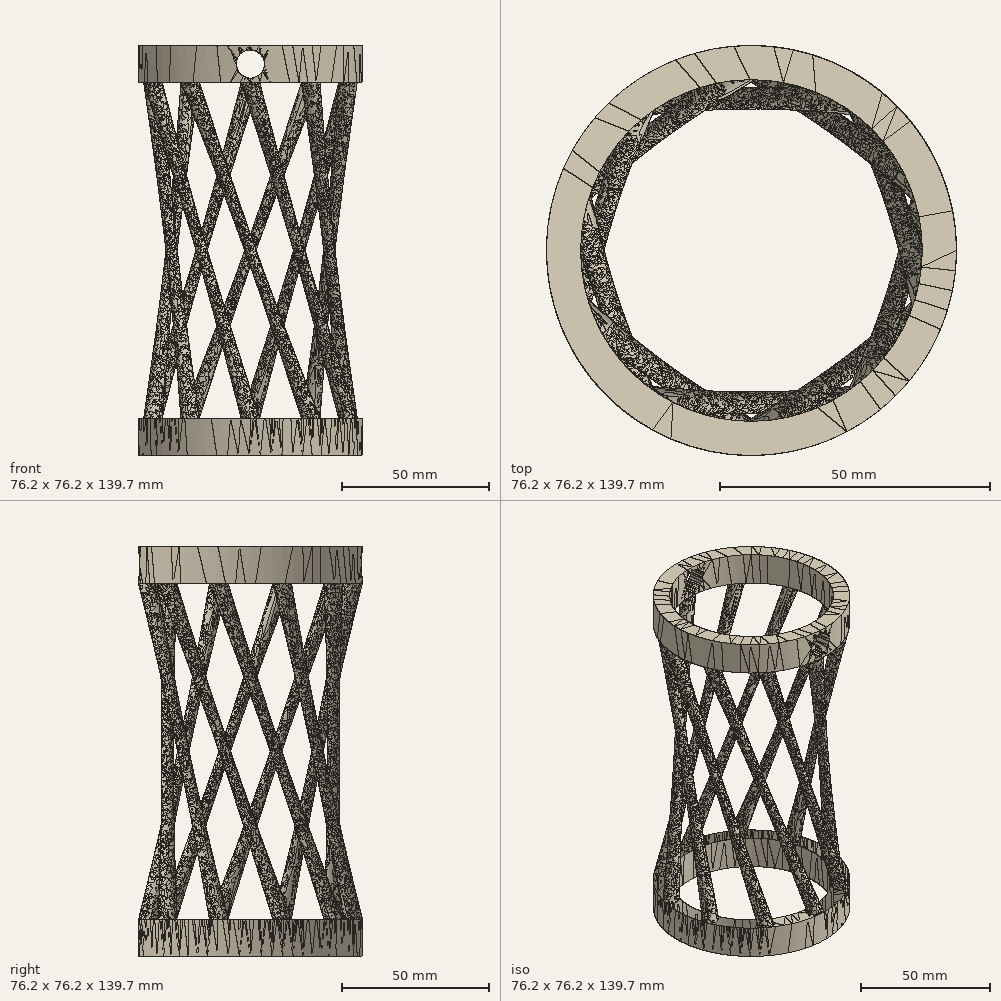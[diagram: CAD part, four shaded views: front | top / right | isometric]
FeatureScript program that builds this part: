
annotation { "Feature Type Name" : "Feature", "Feature Type Description" : "" }
export const myFeature = defineFeature(function(context is Context, id is Id, definition is map)
    precondition{}
    {
        {
            var Q0;
            Q0=qCreatedBy(makeId("Top.planeOp"),FACE);
            var sketch = newSketch(context, id + "F0", { "sketchPlane" : qUnion([Q0])});
            skCircle(sketch, "E0", {"center": v(0, 0) * mm, "radius": 31.75 * mm});
            skCircle(sketch, "E1", {"center": v(0, 0) * mm, "radius": 38.1 * mm});
            skSolve(sketch);
        }
        {
            var Q0;
            Q0 = qSketchRegion(id + "F0", true);
            extrude(context, id + "F1", {"entities" : qUnion([Q0]), "depth" : 12.7 * mm});
        }
        {
            var Q0;
            Q0=qCreatedBy(makeId("Top.planeOp"),FACE);
            cPlane(context, id + "F2", {"entities" : qUnion([Q0]), "cplaneType" : CPlaneType.OFFSET, "offset" : 127 * mm, "width" : 152.4 * mm, "height" : 152.4 * mm});
        }
        {
            var Q0;
            Q0=qCreatedBy(id+"F2.planeOp",FACE);
            var sketch = newSketch(context, id + "F3", { "sketchPlane" : qUnion([Q0])});
            skCircle(sketch, "E2", {"center": v(0, 0) * mm, "radius": 38.1 * mm});
            skCircle(sketch, "E3", {"center": v(0, 0) * mm, "radius": 31.75 * mm});
            skCircle(sketch, "E4", {"center": v(0, 34.92) * mm, "radius": 3.18 * mm});
            skCircle(sketch, "E5.1.0", {"center": v(-20.53, 28.25) * mm, "radius": 3.18 * mm});
            skCircle(sketch, "E5.2.0", {"center": v(-33.22, 10.8) * mm, "radius": 3.18 * mm});
            skCircle(sketch, "E5.3.0", {"center": v(-33.22, -10.8) * mm, "radius": 3.18 * mm});
            skCircle(sketch, "E5.4.0", {"center": v(-20.53, -28.25) * mm, "radius": 3.17 * mm});
            skCircle(sketch, "E5.5.0", {"center": v(0, -34.93) * mm, "radius": 3.18 * mm});
            skCircle(sketch, "E5.6.0", {"center": v(20.53, -28.25) * mm, "radius": 3.17 * mm});
            skCircle(sketch, "E5.7.0", {"center": v(33.22, -10.8) * mm, "radius": 3.17 * mm});
            skCircle(sketch, "E5.8.0", {"center": v(33.22, 10.8) * mm, "radius": 3.17 * mm});
            skCircle(sketch, "E5.9.0", {"center": v(20.53, 28.25) * mm, "radius": 3.18 * mm});
            skSolve(sketch);
        }
        {
            var Q0;
            Q0=makeQuery(id+"F1.opExtrude","CAP_FACE",FACE,{"disambiguationData":[OSD([sQuery(id+"F0.wireOp",EDGE,"E0"),sQuery(id+"F0.wireOp",EDGE,"E1")])],"isStart":false});
            var sketch = newSketch(context, id + "F4", { "sketchPlane" : qUnion([Q0])});
            skCircle(sketch, "E6", {"center": v(0, -34.93) * mm, "radius": 3.18 * mm});
            skCircle(sketch, "E7.1.0", {"center": v(20.53, -28.25) * mm, "radius": 3.18 * mm});
            skCircle(sketch, "E7.2.0", {"center": v(33.22, -10.8) * mm, "radius": 3.18 * mm});
            skCircle(sketch, "E7.3.0", {"center": v(33.22, 10.8) * mm, "radius": 3.18 * mm});
            skCircle(sketch, "E7.4.0", {"center": v(20.53, 28.25) * mm, "radius": 3.17 * mm});
            skCircle(sketch, "E7.5.0", {"center": v(0, 34.93) * mm, "radius": 3.18 * mm});
            skCircle(sketch, "E7.6.0", {"center": v(-20.53, 28.25) * mm, "radius": 3.17 * mm});
            skCircle(sketch, "E7.7.0", {"center": v(-33.22, 10.8) * mm, "radius": 3.17 * mm});
            skCircle(sketch, "E7.8.0", {"center": v(-33.22, -10.8) * mm, "radius": 3.17 * mm});
            skCircle(sketch, "E7.9.0", {"center": v(-20.53, -28.25) * mm, "radius": 3.18 * mm});
            skPoint(sketch, "E7.center", {"position": v(0, 0) * mm});
            skSolve(sketch);
        }
        {
            var Q0;
            Q0=qCreatedBy(makeId("Front.planeOp"),FACE);
            var sketch = newSketch(context, id + "F5", { "sketchPlane" : qUnion([Q0])});
            skFitSpline(sketch, "E8", {"points": [v(0, 12.63) * mm, v(0, 101.58) * mm], "startDerivative": vector(-15.73, 55.47) * mm, "endDerivative": vector(21.79, 104) * mm});
            skFitSpline(sketch, "E9.0", {"points": [v(-13.75, 8.73) * mm, v(-14.53, 11.5) * mm, v(-15.91, 17.44) * mm, v(-17.5, 27.5) * mm, v(-18.57, 38.63) * mm, v(-19.25, 54.7) * mm, v(-18.55, 76.66) * mm, v(-15.93, 95.23) * mm, v(-13.98, 104.51) * mm]});
            skLineSegment(sketch, "E10", {"start": v(0, 101.58) * mm, "end": v(0, 0) * mm, "construction": true});
            skSolve(sketch);
        }
        {
            var Q1;
            {var subQ0=sQuery(id+"F3.wireOp",EDGE,"E5.2.0");var subQ2=makeQuery(id+"F3.imprint","INTERSECT",VERTEX,{"derivedFrom":[sQuery(id+"F3.wireOp",EDGE,"E2"),subQ0]});Q1=makeQuery(id+"F3.imprint","IMPRINT",FACE,{"disambiguationData":[TD([[makeQuery(id+"F3.imprint","IMPRINT",EDGE,{"disambiguationData":[TD([[subQ2,-1.0]])],"derivedFrom":subQ0}),1.0]])]});}
            var Q2;
            {var subQ0=sQuery(id+"F4.wireOp",EDGE,"E7.9.0");var subQ2=makeQuery(id+"F4.imprint","INTERSECT",VERTEX,{"derivedFrom":[makeQuery(id+"F1.opExtrude","CAP_EDGE",EDGE,{"disambiguationData":[OSD([sQuery(id+"F0.wireOp",EDGE,"E1")])],"isStart":false}),subQ0]});Q2=makeQuery(id+"F4.imprint","IMPRINT",FACE,{"disambiguationData":[TD([[makeQuery(id+"F4.imprint","IMPRINT",EDGE,{"disambiguationData":[TD([[subQ2,1.0]])],"derivedFrom":subQ0}),1.0]])]});}
            var Q3;
            Q3=sQuery(id+"F5.wireOp",EDGE,"E9.0");
            loft(context, id + "F6", {"operationType" : NewBodyOperationType.ADD, "sheetProfilesArray" : [{ "sheetProfileEntities" : qUnion([Q1]) }, { "sheetProfileEntities" : qUnion([Q2]) }], "guidesArray" : [{ "guideEntities" : qUnion([Q3]), "guideDerivativeType" : LoftGuideDerivativeType.DEFAULT, "guideDerivativeMagnitude" : 1 }]});
        }
        {
            var Q0;
            Q0=makeQuery(id+"F1.opExtrude","SWEPT_BODY",BODY,{"disambiguationData":[OSD([sQuery(id+"F0.wireOp",EDGE,"E0"),sQuery(id+"F0.wireOp",EDGE,"E1")])]});
            var Q1;
            Q1=sQuery(id+"F5.wireOp",EDGE,"E10");
            circularPattern(context, id + "F7", {"operationType" : NewBodyOperationType.ADD, "entities" : qUnion([Q0]), "axis" : qUnion([Q1]), "angle" : 360 * degree, "instanceCount" : 10, "equalSpace" : true});
        }
        {
            var Q0;
            {var subQ3=sQuery(id+"F3.wireOp",EDGE,"E2");var subQ5=sQuery(id+"F3.wireOp",EDGE,"E5.2.0");var subQ7=makeQuery(id+"F3.imprint","INTERSECT",VERTEX,{"derivedFrom":[subQ3,subQ5]});Q0=makeQuery(id+"F3.imprint","IMPRINT",FACE,{"disambiguationData":[TD([[makeQuery(id+"F3.imprint","IMPRINT",EDGE,{"disambiguationData":[TD([[subQ7,-1.0]])],"derivedFrom":subQ3}),1.0]])]});}
            var Q1;
            {var subQ3=sQuery(id+"F3.wireOp",EDGE,"E2");var subQ5=sQuery(id+"F3.wireOp",EDGE,"E5.1.0");var subQ7=makeQuery(id+"F3.imprint","INTERSECT",VERTEX,{"derivedFrom":[subQ3,subQ5]});Q1=makeQuery(id+"F3.imprint","IMPRINT",FACE,{"disambiguationData":[TD([[makeQuery(id+"F3.imprint","IMPRINT",EDGE,{"disambiguationData":[TD([[subQ7,-1.0]])],"derivedFrom":subQ3}),1.0]])]});}
            var Q2;
            {var subQ3=sQuery(id+"F3.wireOp",EDGE,"E2");var subQ5=sQuery(id+"F3.wireOp",EDGE,"E4");var subQ7=makeQuery(id+"F3.imprint","INTERSECT",VERTEX,{"derivedFrom":[subQ3,subQ5]});Q2=makeQuery(id+"F3.imprint","IMPRINT",FACE,{"disambiguationData":[TD([[makeQuery(id+"F3.imprint","IMPRINT",EDGE,{"disambiguationData":[TD([[subQ7,-1.0]])],"derivedFrom":subQ3}),1.0]])]});}
            var Q3;
            {var subQ0=sQuery(id+"F3.wireOp",EDGE,"E5.3.0");var subQ2=makeQuery(id+"F3.imprint","INTERSECT",VERTEX,{"derivedFrom":[sQuery(id+"F3.wireOp",EDGE,"E2"),subQ0]});Q3=makeQuery(id+"F3.imprint","IMPRINT",FACE,{"disambiguationData":[TD([[makeQuery(id+"F3.imprint","IMPRINT",EDGE,{"disambiguationData":[TD([[subQ2,-1.0]])],"derivedFrom":subQ0}),1.0]])]});}
            var Q4;
            {var subQ3=sQuery(id+"F3.wireOp",EDGE,"E2");var subQ5=sQuery(id+"F3.wireOp",EDGE,"E5.3.0");var subQ7=makeQuery(id+"F3.imprint","INTERSECT",VERTEX,{"derivedFrom":[subQ3,subQ5]});Q4=makeQuery(id+"F3.imprint","IMPRINT",FACE,{"disambiguationData":[TD([[makeQuery(id+"F3.imprint","IMPRINT",EDGE,{"disambiguationData":[TD([[subQ7,-1.0]])],"derivedFrom":subQ3}),1.0]])]});}
            var Q5;
            {var subQ0=sQuery(id+"F3.wireOp",EDGE,"E5.4.0");var subQ2=makeQuery(id+"F3.imprint","INTERSECT",VERTEX,{"derivedFrom":[sQuery(id+"F3.wireOp",EDGE,"E2"),subQ0]});Q5=makeQuery(id+"F3.imprint","IMPRINT",FACE,{"disambiguationData":[TD([[makeQuery(id+"F3.imprint","IMPRINT",EDGE,{"disambiguationData":[TD([[subQ2,-1.0]])],"derivedFrom":subQ0}),1.0]])]});}
            var Q6;
            {var subQ3=sQuery(id+"F3.wireOp",EDGE,"E2");var subQ5=sQuery(id+"F3.wireOp",EDGE,"E5.4.0");var subQ7=makeQuery(id+"F3.imprint","INTERSECT",VERTEX,{"derivedFrom":[subQ3,subQ5]});Q6=makeQuery(id+"F3.imprint","IMPRINT",FACE,{"disambiguationData":[TD([[makeQuery(id+"F3.imprint","IMPRINT",EDGE,{"disambiguationData":[TD([[subQ7,-1.0]])],"derivedFrom":subQ3}),1.0]])]});}
            var Q7;
            {var subQ0=sQuery(id+"F3.wireOp",EDGE,"E5.2.0");var subQ2=makeQuery(id+"F3.imprint","INTERSECT",VERTEX,{"derivedFrom":[sQuery(id+"F3.wireOp",EDGE,"E2"),subQ0]});Q7=makeQuery(id+"F3.imprint","IMPRINT",FACE,{"disambiguationData":[TD([[makeQuery(id+"F3.imprint","IMPRINT",EDGE,{"disambiguationData":[TD([[subQ2,-1.0]])],"derivedFrom":subQ0}),1.0]])]});}
            var Q8;
            {var subQ0=sQuery(id+"F3.wireOp",EDGE,"E5.1.0");var subQ2=makeQuery(id+"F3.imprint","INTERSECT",VERTEX,{"derivedFrom":[sQuery(id+"F3.wireOp",EDGE,"E2"),subQ0]});Q8=makeQuery(id+"F3.imprint","IMPRINT",FACE,{"disambiguationData":[TD([[makeQuery(id+"F3.imprint","IMPRINT",EDGE,{"disambiguationData":[TD([[subQ2,-1.0]])],"derivedFrom":subQ0}),1.0]])]});}
            var Q9;
            {var subQ0=sQuery(id+"F3.wireOp",EDGE,"E4");var subQ2=makeQuery(id+"F3.imprint","INTERSECT",VERTEX,{"derivedFrom":[sQuery(id+"F3.wireOp",EDGE,"E2"),subQ0]});Q9=makeQuery(id+"F3.imprint","IMPRINT",FACE,{"disambiguationData":[TD([[makeQuery(id+"F3.imprint","IMPRINT",EDGE,{"disambiguationData":[TD([[subQ2,-1.0]])],"derivedFrom":subQ0}),1.0]])]});}
            var Q10;
            {var subQ3=sQuery(id+"F3.wireOp",EDGE,"E2");var subQ5=sQuery(id+"F3.wireOp",EDGE,"E5.9.0");var subQ7=makeQuery(id+"F3.imprint","INTERSECT",VERTEX,{"derivedFrom":[subQ3,subQ5]});Q10=makeQuery(id+"F3.imprint","IMPRINT",FACE,{"disambiguationData":[TD([[makeQuery(id+"F3.imprint","IMPRINT",EDGE,{"disambiguationData":[TD([[subQ7,-1.0]])],"derivedFrom":subQ3}),1.0]])]});}
            var Q11;
            {var subQ0=sQuery(id+"F3.wireOp",EDGE,"E5.9.0");var subQ2=makeQuery(id+"F3.imprint","INTERSECT",VERTEX,{"derivedFrom":[sQuery(id+"F3.wireOp",EDGE,"E2"),subQ0]});Q11=makeQuery(id+"F3.imprint","IMPRINT",FACE,{"disambiguationData":[TD([[makeQuery(id+"F3.imprint","IMPRINT",EDGE,{"disambiguationData":[TD([[subQ2,-1.0]])],"derivedFrom":subQ0}),1.0]])]});}
            var Q12;
            {var subQ0=sQuery(id+"F3.wireOp",EDGE,"E5.9.0");var subQ3=sQuery(id+"F3.wireOp",EDGE,"E2");var subQ4=makeQuery(id+"F3.imprint","INTERSECT",VERTEX,{"derivedFrom":[subQ3,subQ0]});Q12=makeQuery(id+"F3.imprint","IMPRINT",FACE,{"disambiguationData":[TD([[makeQuery(id+"F3.imprint","IMPRINT",EDGE,{"disambiguationData":[TD([[subQ4,1.0]])],"derivedFrom":subQ3}),1.0]])]});}
            var Q13;
            {var subQ0=sQuery(id+"F3.wireOp",EDGE,"E5.8.0");var subQ2=makeQuery(id+"F3.imprint","INTERSECT",VERTEX,{"derivedFrom":[sQuery(id+"F3.wireOp",EDGE,"E2"),subQ0]});Q13=makeQuery(id+"F3.imprint","IMPRINT",FACE,{"disambiguationData":[TD([[makeQuery(id+"F3.imprint","IMPRINT",EDGE,{"disambiguationData":[TD([[subQ2,-1.0]])],"derivedFrom":subQ0}),1.0]])]});}
            var Q14;
            {var subQ0=sQuery(id+"F3.wireOp",EDGE,"E5.8.0");var subQ3=sQuery(id+"F3.wireOp",EDGE,"E2");var subQ4=makeQuery(id+"F3.imprint","INTERSECT",VERTEX,{"derivedFrom":[subQ3,subQ0]});Q14=makeQuery(id+"F3.imprint","IMPRINT",FACE,{"disambiguationData":[TD([[makeQuery(id+"F3.imprint","IMPRINT",EDGE,{"disambiguationData":[TD([[subQ4,1.0]])],"derivedFrom":subQ3}),1.0]])]});}
            var Q15;
            {var subQ0=sQuery(id+"F3.wireOp",EDGE,"E5.7.0");var subQ2=makeQuery(id+"F3.imprint","INTERSECT",VERTEX,{"derivedFrom":[sQuery(id+"F3.wireOp",EDGE,"E2"),subQ0]});Q15=makeQuery(id+"F3.imprint","IMPRINT",FACE,{"disambiguationData":[TD([[makeQuery(id+"F3.imprint","IMPRINT",EDGE,{"disambiguationData":[TD([[subQ2,-1.0]])],"derivedFrom":subQ0}),1.0]])]});}
            var Q16;
            {var subQ3=sQuery(id+"F3.wireOp",EDGE,"E2");var subQ5=sQuery(id+"F3.wireOp",EDGE,"E5.6.0");var subQ7=makeQuery(id+"F3.imprint","INTERSECT",VERTEX,{"derivedFrom":[subQ3,subQ5]});Q16=makeQuery(id+"F3.imprint","IMPRINT",FACE,{"disambiguationData":[TD([[makeQuery(id+"F3.imprint","IMPRINT",EDGE,{"disambiguationData":[TD([[subQ7,-1.0]])],"derivedFrom":subQ3}),1.0]])]});}
            var Q17;
            {var subQ0=sQuery(id+"F3.wireOp",EDGE,"E5.6.0");var subQ2=makeQuery(id+"F3.imprint","INTERSECT",VERTEX,{"derivedFrom":[sQuery(id+"F3.wireOp",EDGE,"E2"),subQ0]});Q17=makeQuery(id+"F3.imprint","IMPRINT",FACE,{"disambiguationData":[TD([[makeQuery(id+"F3.imprint","IMPRINT",EDGE,{"disambiguationData":[TD([[subQ2,-1.0]])],"derivedFrom":subQ0}),1.0]])]});}
            var Q18;
            {var subQ3=sQuery(id+"F3.wireOp",EDGE,"E2");var subQ5=sQuery(id+"F3.wireOp",EDGE,"E5.5.0");var subQ7=makeQuery(id+"F3.imprint","INTERSECT",VERTEX,{"derivedFrom":[subQ3,subQ5]});Q18=makeQuery(id+"F3.imprint","IMPRINT",FACE,{"disambiguationData":[TD([[makeQuery(id+"F3.imprint","IMPRINT",EDGE,{"disambiguationData":[TD([[subQ7,-1.0]])],"derivedFrom":subQ3}),1.0]])]});}
            var Q19;
            {var subQ0=sQuery(id+"F3.wireOp",EDGE,"E5.5.0");var subQ2=makeQuery(id+"F3.imprint","INTERSECT",VERTEX,{"derivedFrom":[sQuery(id+"F3.wireOp",EDGE,"E2"),subQ0]});Q19=makeQuery(id+"F3.imprint","IMPRINT",FACE,{"disambiguationData":[TD([[makeQuery(id+"F3.imprint","IMPRINT",EDGE,{"disambiguationData":[TD([[subQ2,-1.0]])],"derivedFrom":subQ0}),1.0]])]});}
            extrude(context, id + "F8", {"entities" : qUnion([Q0, Q1, Q2, Q3, Q4, Q5, Q6, Q7, Q8, Q9, Q10, Q11, Q12, Q13, Q14, Q15, Q16, Q17, Q18, Q19]), "operationType" : NewBodyOperationType.ADD, "depth" : 12.7 * mm});
        }
        {
            var Q0;
            Q0=qCreatedBy(makeId("Front.planeOp"),FACE);
            var sketch = newSketch(context, id + "F9", { "sketchPlane" : qUnion([Q0])});
            skLineSegment(sketch, "E11", {"start": v(0, 112.19) * mm, "end": v(0, -36.63) * mm, "construction": true});
            skLineSegment(sketch, "E12", {"start": v(-44.62, 69.85) * mm, "end": v(76.45, 69.85) * mm, "construction": true});
            skCircle(sketch, "E13", {"center": v(0, 133.35) * mm, "radius": 4.76 * mm});
            skCircle(sketch, "E14.MirrorC", {"center": v(0, 6.35) * mm, "radius": 4.76 * mm});
            skLineSegment(sketch, "E15", {"start": v(0, 178.6) * mm, "end": v(0, 207.17) * mm, "construction": true});
            skLineSegment(sketch, "E16", {"start": v(-27.53, 133.35) * mm, "end": v(32.09, 133.35) * mm, "construction": true});
            skSolve(sketch);
        }
        {
            var Q0;
            Q0=makeQuery(id+"F9.imprint","IMPRINT",FACE,{"disambiguationData":[TD([[makeQuery(id+"F9.imprint","IMPRINT",EDGE,{"derivedFrom":sQuery(id+"F9.wireOp",EDGE,"E13")}),1.0]])]});
            var Q1;
            Q1=makeQuery(id+"F9.imprint","IMPRINT",FACE,{"disambiguationData":[TD([[makeQuery(id+"F9.imprint","IMPRINT",EDGE,{"derivedFrom":sQuery(id+"F9.wireOp",EDGE,"E14.MirrorC")}),-1.0]])]});
            extrude(context, id + "F10", {"entities" : qUnion([Q0, Q1]), "operationType" : NewBodyOperationType.REMOVE, "endBound" : BoundingType.THROUGH_ALL, "oppositeDirection" : true, "depth" : 101.6 * mm, "hasSecondDirection" : true, "secondDirectionBound" : SecondDirectionBoundingType.THROUGH_ALL, "secondDirectionOppositeDirection" : false, "secondDirectionDepth" : 25.4 * mm});
        }
        {
            var Q0;
            Q0=makeQuery(id+"F1.opExtrude","SWEPT_BODY",BODY,{"disambiguationData":[OSD([sQuery(id+"F0.wireOp",EDGE,"E0"),sQuery(id+"F0.wireOp",EDGE,"E1")])]});
            transform(context, id + "F11", {"entities" : qUnion([Q0]), "transformType" : TransformType.TRANSLATION_3D, "dx" : 0 * mm, "dy" : 0 * mm, "dz" : 0 * mm, "makeCopy" : true});
        }
    });
